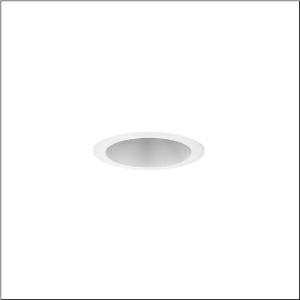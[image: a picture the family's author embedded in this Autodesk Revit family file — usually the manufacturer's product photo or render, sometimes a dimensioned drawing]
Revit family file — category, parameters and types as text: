
# Revit family: lunis_31_mini_51dn15de31
name_source: partatom
category: Lighting Fixtures
units: mm (PartAtom-declared; Revit-internal decimal feet)

## family parameters
Cut with Voids When Loaded = No
Host = Face
Light Source = No
Part Type = Normal
Room Calculation Point = No
Round Connector Dimension = Use Diameter
Shared = No

## types (1)
- Lunis 31 mini (1 x LED, 1000 lm, 8.3 W, 3000K)
    Apparent Load = 8 VA
    CIE Flux Codes = 93 98 100 100 100
    Color Rendering = 80
    Color Temperature = 3000K
    Default Elevation = 1800 mm
    Description = Lunis 31,  mini, downlight, light control with lens, light emission: direct distribution, LED rated luminous flux: 1.000lm, light colour: 830, mains connection: 220..240V, AC, 50/60Hz, housing, white, protection rating (complete): IP20, protection rating (on room side): IP54, insulation class (complete): insulation class II (safety insulation), certification: CE, packaging unit: 1 piece
    Height = 0 mm  [stored 0 ft]
    Lamp = 1 x LED
    Lamp Light Flux = 1000 lm
    Lamp Power = 8.3 W
    Lamp count = 1
    Length = 188 mm  [stored 0.616798 ft]
    Luminous efficacy = 120 lm/W
    Manufacturer = Siteco
    ModVariant = No
    Model = 51DN15DE31
    Mounting Place = Ceiling
    Mounting Type = Recessed
    Number of Poles = 1
    OnlyDefault = Yes
    Power Factor = 1
    Product Name = Lunis 31 mini
    Product group = downlight
    ProductGroupID = 400
    Protection Class = Protection class II
    Protection Degree = IP 20
    RLX_Detail_Level = 1
    RLX_Emergency_Light_Flux = 0 lm
    RLX_Emergency_Type = 0
    RLX_Emergency_Type_DB = No
    RlxData = <blob elided: 21789 chars, md5=621deefd>
    Socket = socket
    Standby Power = 0 W
    System Light Flux = 1000 lm
    System Power = 8 W
    Type Comments = Product without accessories
    Type Image = l_1005624.jpg
    URL = http://relux.com
    VarID = ---
    Voltage = 0 V
    Weight = 0.00 kg
    Width = 0 mm  [stored 0 ft]

note: [stored X ft] marks values corroborated as IEEE doubles in the binary element streams (Revit-internal decimal feet)

## geometry (parser evidence)
native form markers: Blend x4, Sweep x11
no freeform markers — native parametric forms only
